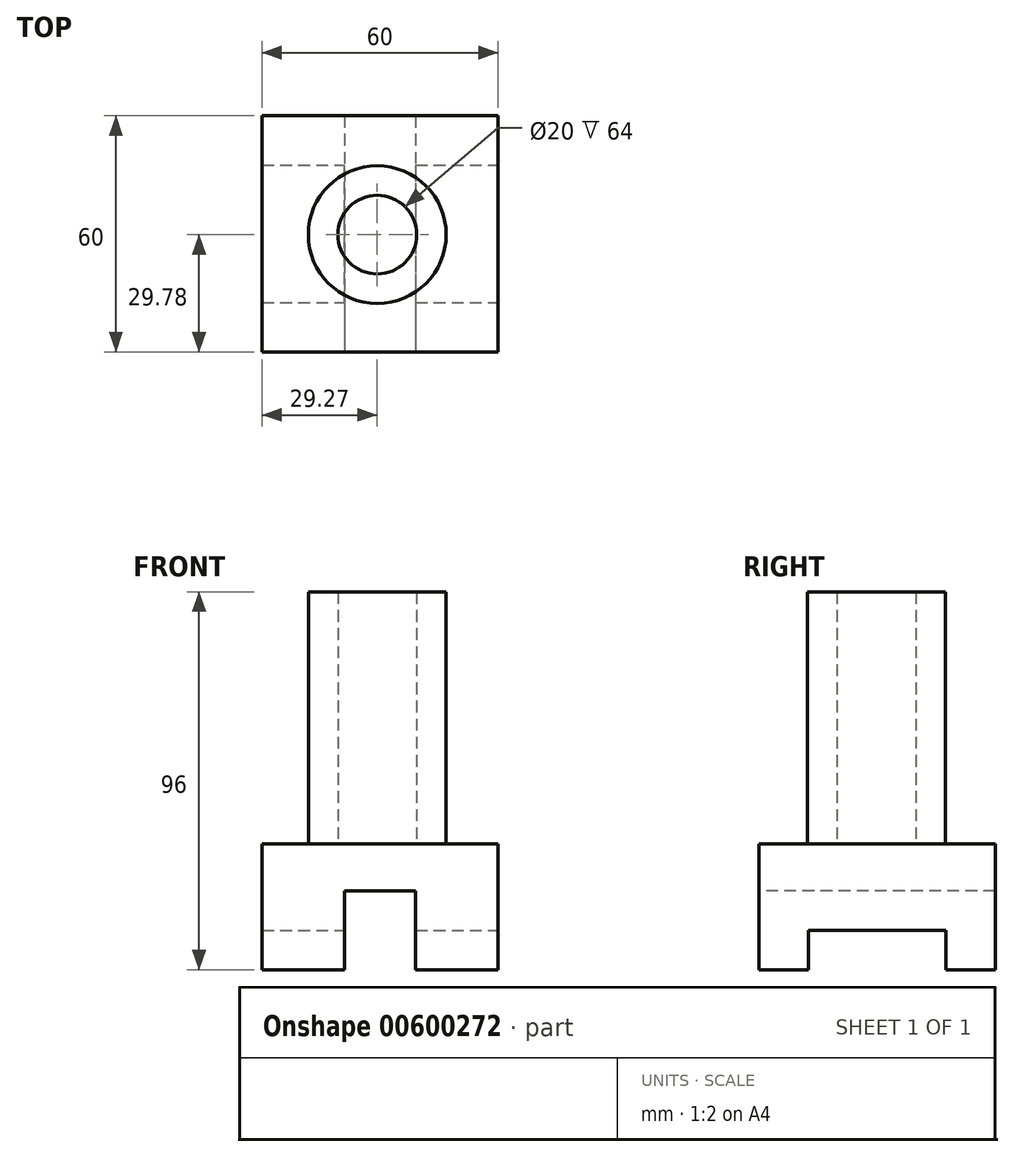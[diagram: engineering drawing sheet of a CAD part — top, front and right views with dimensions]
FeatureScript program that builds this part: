
annotation { "Feature Type Name" : "Feature", "Feature Type Description" : "" }
export const myFeature = defineFeature(function(context is Context, id is Id, definition is map)
    precondition{}
    {
        {
            var Q0;
            Q0=qCreatedBy(makeId("Top.planeOp"),FACE);
            var sketch = newSketch(context, id + "F0", { "sketchPlane" : qUnion([Q0])});
            skLineSegment(sketch, "E0.bottom", {"start": v(30.73, -29.78) * mm, "end": v(-29.27, -29.78) * mm});
            skLineSegment(sketch, "E0.top", {"start": v(30.73, 30.22) * mm, "end": v(-29.27, 30.22) * mm});
            skLineSegment(sketch, "E0.left", {"start": v(30.73, -29.78) * mm, "end": v(30.73, 30.22) * mm});
            skLineSegment(sketch, "E0.right", {"start": v(-29.27, -29.78) * mm, "end": v(-29.27, 30.22) * mm});
            skSolve(sketch);
        }
        {
            var Q0;
            Q0 = qSketchRegion(id + "F0", true);
            extrude(context, id + "F1", {"entities" : qUnion([Q0]), "depth" : 32 * mm, "offsetDistance" : 25 * mm});
        }
        {
            var Q0;
            Q0=makeQuery(id+"F1.opExtrude","SWEPT_FACE",FACE,{"disambiguationData":[OSD([sQuery(id+"F0.wireOp",EDGE,"E0.bottom")])]});
            var sketch = newSketch(context, id + "F2", { "sketchPlane" : qUnion([Q0])});
            skLineSegment(sketch, "E1", {"start": v(-8.27, 0) * mm, "end": v(-8.27, 20) * mm});
            skLineSegment(sketch, "E2", {"start": v(-8.27, 20) * mm, "end": v(9.73, 20) * mm});
            skLineSegment(sketch, "E3", {"start": v(9.73, 20) * mm, "end": v(9.73, 0) * mm});
            skLineSegment(sketch, "E4", {"start": v(9.73, 0) * mm, "end": v(-8.27, 0) * mm});
            skSolve(sketch);
        }
        {
            var Q0;
            Q0 = qSketchRegion(id + "F2", true);
            extrude(context, id + "F3", {"entities" : qUnion([Q0]), "operationType" : NewBodyOperationType.REMOVE, "endBound" : BoundingType.THROUGH_ALL, "oppositeDirection" : true, "depth" : 25 * mm, "offsetDistance" : 25 * mm});
        }
        {
            var Q0;
            Q0=makeQuery(id+"F1.opExtrude","SWEPT_FACE",FACE,{"disambiguationData":[OSD([sQuery(id+"F0.wireOp",EDGE,"E0.left")])]});
            var sketch = newSketch(context, id + "F4", { "sketchPlane" : qUnion([Q0])});
            skLineSegment(sketch, "E5", {"start": v(-17.28, 0) * mm, "end": v(-17.28, 10) * mm});
            skLineSegment(sketch, "E6", {"start": v(-17.28, 10) * mm, "end": v(17.72, 10) * mm});
            skLineSegment(sketch, "E7", {"start": v(17.72, 10) * mm, "end": v(17.72, 0) * mm});
            skLineSegment(sketch, "E8", {"start": v(17.72, 0) * mm, "end": v(-17.28, 0) * mm});
            skSolve(sketch);
        }
        {
            var Q0;
            Q0=makeQuery(id+"F4.imprint","IMPRINT",FACE,{"disambiguationData":[TD([[makeQuery(id+"F4.imprint","IMPRINT",EDGE,{"derivedFrom":sQuery(id+"F4.wireOp",EDGE,"E5")}),-1.0]])]});
            extrude(context, id + "F5", {"entities" : qUnion([Q0]), "operationType" : NewBodyOperationType.REMOVE, "endBound" : BoundingType.THROUGH_ALL, "oppositeDirection" : true, "depth" : 25 * mm, "offsetDistance" : 25 * mm});
        }
        {
            var Q0;
            Q0=makeQuery(id+"F1.opExtrude","CAP_FACE",FACE,{"disambiguationData":[OSD([sQuery(id+"F0.wireOp",EDGE,"E0.bottom"),sQuery(id+"F0.wireOp",EDGE,"E0.top"),sQuery(id+"F0.wireOp",EDGE,"E0.left"),sQuery(id+"F0.wireOp",EDGE,"E0.right")])],"isStart":false});
            var sketch = newSketch(context, id + "F6", { "sketchPlane" : qUnion([Q0])});
            skCircle(sketch, "E9", {"center": v(0, 0) * mm, "radius": 17.5 * mm});
            skCircle(sketch, "E10", {"center": v(0, 0) * mm, "radius": 10 * mm});
            skSolve(sketch);
        }
        {
            var Q0;
            Q0 = qSketchRegion(id + "F6", true);
            extrude(context, id + "F7", {"entities" : qUnion([Q0]), "operationType" : NewBodyOperationType.ADD, "depth" : 64 * mm, "offsetDistance" : 25 * mm});
        }
    });
